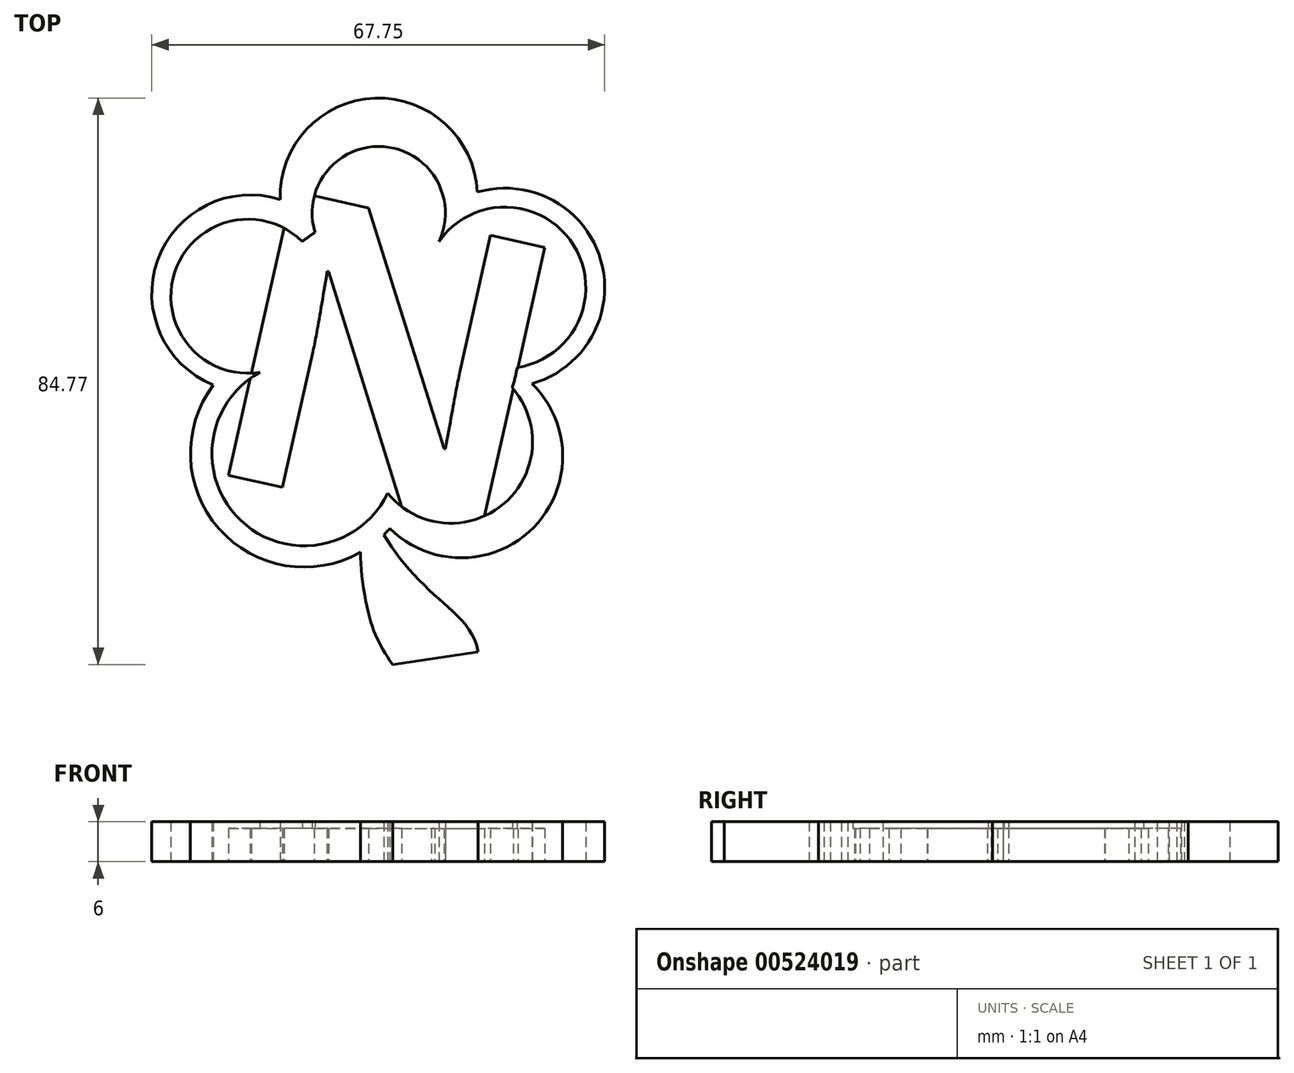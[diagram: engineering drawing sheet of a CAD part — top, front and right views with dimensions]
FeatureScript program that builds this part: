
annotation { "Feature Type Name" : "Feature", "Feature Type Description" : "" }
export const myFeature = defineFeature(function(context is Context, id is Id, definition is map)
    precondition{}
    {
        {
            var Q0;
            Q0=qCreatedBy(makeId("Top.planeOp"),FACE);
            var sketch = newSketch(context, id + "F0", { "sketchPlane" : qUnion([Q0])});
            skArc(sketch, "E0", {"start": v(22.9, -8.06) * mm, "mid": v(33.24, 10.38) * mm, "end": v(14.74, 20.6) * mm});
            skArc(sketch, "E1", {"start": v(-24.75, -8.26) * mm, "mid": v(-21.87, -31.71) * mm, "end": v(1.67, -29.71) * mm});
            skArc(sketch, "E2", {"start": v(1.67, -29.71) * mm, "mid": v(23.19, -29.57) * mm, "end": v(22.9, -8.06) * mm});
            skArc(sketch, "E3", {"start": v(-11.45, 13.21) * mm, "mid": v(-30.54, 8.57) * mm, "end": v(-17.77, -6.36) * mm});
            skArc(sketch, "E4", {"start": v(8.06, 11.62) * mm, "mid": v(1.64, 27.3) * mm, "end": v(-9.52, 14.55) * mm});
            skArc(sketch, "E5", {"start": v(20.7, -5.64) * mm, "mid": v(28.65, 13.43) * mm, "end": v(8.06, 11.62) * mm});
            skArc(sketch, "E6", {"start": v(-17.77, -6.36) * mm, "mid": v(-19.86, -29.22) * mm, "end": v(2.1, -22.5) * mm});
            skArc(sketch, "E7.trimOffspring", {"start": v(-14.75, 19.52) * mm, "mid": v(-33.08, 10.43) * mm, "end": v(-24.75, -8.26) * mm});
            skArc(sketch, "E8.trimOffspring", {"start": v(0.07, -22.52) * mm, "mid": v(1.08, -22.54) * mm, "end": v(2.1, -22.5) * mm});
            skArc(sketch, "E9.trimOffspring", {"start": v(19.98, -8.68) * mm, "mid": v(20.4, -7.18) * mm, "end": v(20.7, -5.64) * mm});
            skArc(sketch, "E10.trimOffspring", {"start": v(-9.52, 14.55) * mm, "mid": v(-10.5, 13.91) * mm, "end": v(-11.45, 13.21) * mm});
            skArc(sketch, "E11.trimOffspring", {"start": v(14.74, 20.6) * mm, "mid": v(-0.54, 34.67) * mm, "end": v(-14.75, 19.52) * mm});
            skArc(sketch, "E12.trimOffspring", {"start": v(0.07, -22.52) * mm, "mid": v(17.78, -26.76) * mm, "end": v(19.98, -8.68) * mm});
            skSolve(sketch);
        }
        {
            var Q0;
            Q0=makeQuery(id+"F0.imprint","IMPRINT",FACE,{"disambiguationData":[TD([[makeQuery(id+"F0.imprint","IMPRINT",EDGE,{"derivedFrom":sQuery(id+"F0.wireOp",EDGE,"E0")}),1.0]])]});
            extrude(context, id + "F1", {"entities" : qUnion([Q0]), "depth" : 6 * mm, "offsetDistance" : 25 * mm});
        }
        {
            var Q0;
            Q0=qCreatedBy(makeId("Top.planeOp"),FACE);
            var sketch = newSketch(context, id + "F2", { "sketchPlane" : qUnion([Q0])});
            skText(sketch, "E13", { "text": "N", "fontName": "OpenSans-Bold.ttf"});
            const initialGuessF2  = {"E13": [-0.02783, -0.02055, 0.97562, -0.21945, 0.044]};
            skSetInitialGuess(sketch, initialGuessF2);
            skSolve(sketch);
        }
        {
            var Q0;
            Q0 = qSketchRegion(id + "F2", true);
            extrude(context, id + "F3", {"entities" : qUnion([Q0]), "operationType" : NewBodyOperationType.ADD, "depth" : 5 * mm, "offsetDistance" : 25 * mm});
        }
        {
            var Q0;
            Q0=qCreatedBy(makeId("Top.planeOp"),FACE);
            var sketch = newSketch(context, id + "F4", { "sketchPlane" : qUnion([Q0])});
            skFitSpline(sketch, "E14", {"points": [v(2.07, -50.09) * mm, v(-1.61, -42.05) * mm, v(-2.24, -30.2) * mm, v(0, -29.12) * mm], "startDerivative": vector(-14.37, 20.78) * mm, "endDerivative": vector(14.97, 10.77) * mm});
            skFitSpline(sketch, "E15", {"points": [v(14.89, -48.2) * mm, v(8.74, -40.04) * mm, v(0, -29.12) * mm], "startDerivative": vector(-4.88, 24.47) * mm, "endDerivative": vector(-11.13, 23.67) * mm});
            skLineSegment(sketch, "E16", {"start": v(2.07, -50.09) * mm, "end": v(14.89, -48.2) * mm});
            skSolve(sketch);
        }
        {
            var Q0;
            Q0 = qSketchRegion(id + "F4", true);
            extrude(context, id + "F5", {"entities" : qUnion([Q0]), "operationType" : NewBodyOperationType.ADD, "depth" : 6 * mm, "offsetDistance" : 25 * mm});
        }
    });
